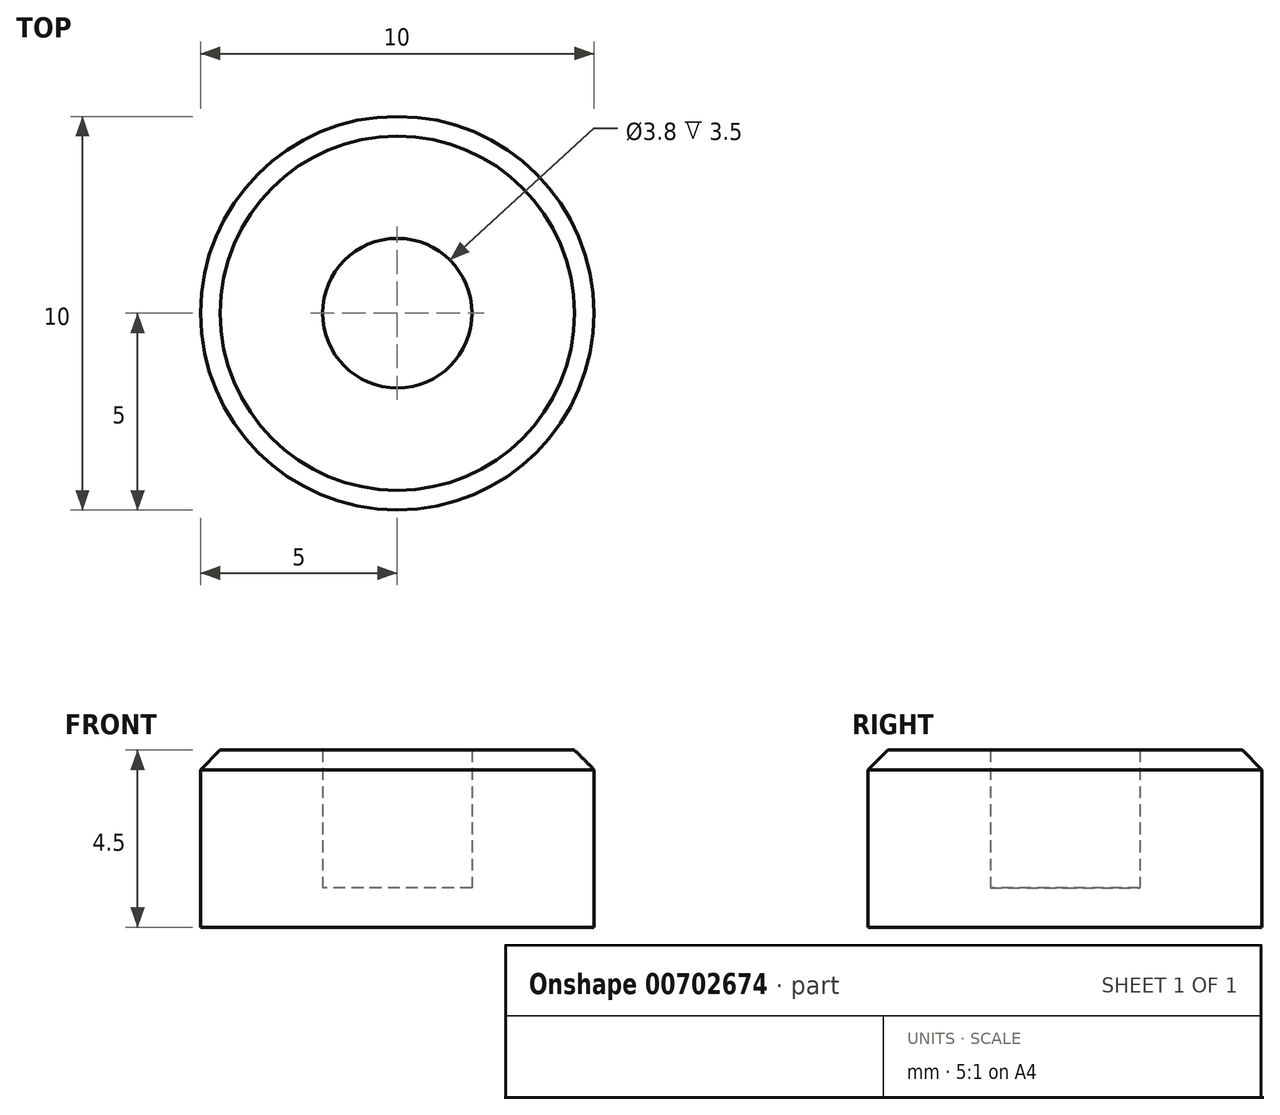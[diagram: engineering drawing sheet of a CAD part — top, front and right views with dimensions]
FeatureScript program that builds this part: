
annotation { "Feature Type Name" : "Feature", "Feature Type Description" : "" }
export const myFeature = defineFeature(function(context is Context, id is Id, definition is map)
    precondition{}
    {
        {
            var Q0;
            Q0=qCreatedBy(makeId("Top.planeOp"),FACE);
            var sketch = newSketch(context, id + "F0", { "sketchPlane" : qUnion([Q0])});
            skCircle(sketch, "E0", {"center": v(0, 0) * mm, "radius": 5 * mm});
            skCircle(sketch, "E1", {"center": v(0, 0) * mm, "radius": 1.9 * mm});
            skSolve(sketch);
        }
        {
            var Q0;
            Q0 = qSketchRegion(id + "F0", true);
            extrude(context, id + "F1", {"entities" : qUnion([Q0]), "depth" : 4.5 * mm, "offsetDistance" : 25 * mm});
        }
        {
            var Q0;
            Q0=makeQuery(id+"F0.imprint","IMPRINT",FACE,{"disambiguationData":[TD([[makeQuery(id+"F0.imprint","IMPRINT",EDGE,{"derivedFrom":sQuery(id+"F0.wireOp",EDGE,"E1")}),1.0]])]});
            extrude(context, id + "F2", {"entities" : qUnion([Q0]), "operationType" : NewBodyOperationType.ADD, "depth" : 1 * mm, "offsetDistance" : 25 * mm});
        }
        {
            var Q0;
            Q0=makeQuery(id+"F1.opExtrude","CAP_EDGE",EDGE,{"disambiguationData":[OSD([sQuery(id+"F0.wireOp",EDGE,"E0")])],"isStart":false});
            chamfer(context, id + "F3", {"entities" : qUnion([Q0]), "width" : .5 * mm, "tangentPropagation" : true});
        }
    });
